# Revit family: Haworth_msit_Table
name_source: partatom
category: Furniture
revit_build: Autodesk Revit 2018 (Build: 20170223_1515(x64)
units: mm (PartAtom-declared; Revit-internal decimal feet)

## family parameters
Always vertical = Yes
Cut with Voids When Loaded = No
OmniClass Number = 23.40.70.14.64.21
OmniClass Title = Systems Furniture
Room Calculation Point = No
Shared = No
Work Plane-Based = No

## types (2) — shared parameters
Assembly Code = E2020200
Description = Haworth m sit Table
Frame Depth = 1 1/4"
Manufacturer = Haworth
Model = TOMS
Revision Number = 5
Size = Verify Final Dim. w/ Haworth
Table Edge Offset = 1"
Table Finish = Haworth _ Glass _ Frosted
URL = http://www.haworth.com
URL - Product = https://www.haworth.com
Warranty = http://www.haworth.com

## per-type parameters (varying)
| type | Actual Depth | Actual Height | Actual Width | Rectangle | Square |
| TOMS - Rectangle | 23 1/2" | 13 3/4" | 47 1/4" | Yes | No |
| TOMS - Square | 19 3/4" | 19 3/4" | 19 3/4" | No | Yes |

## geometry (parser evidence)
native form markers: Sweep x3
no freeform markers — native parametric forms only
